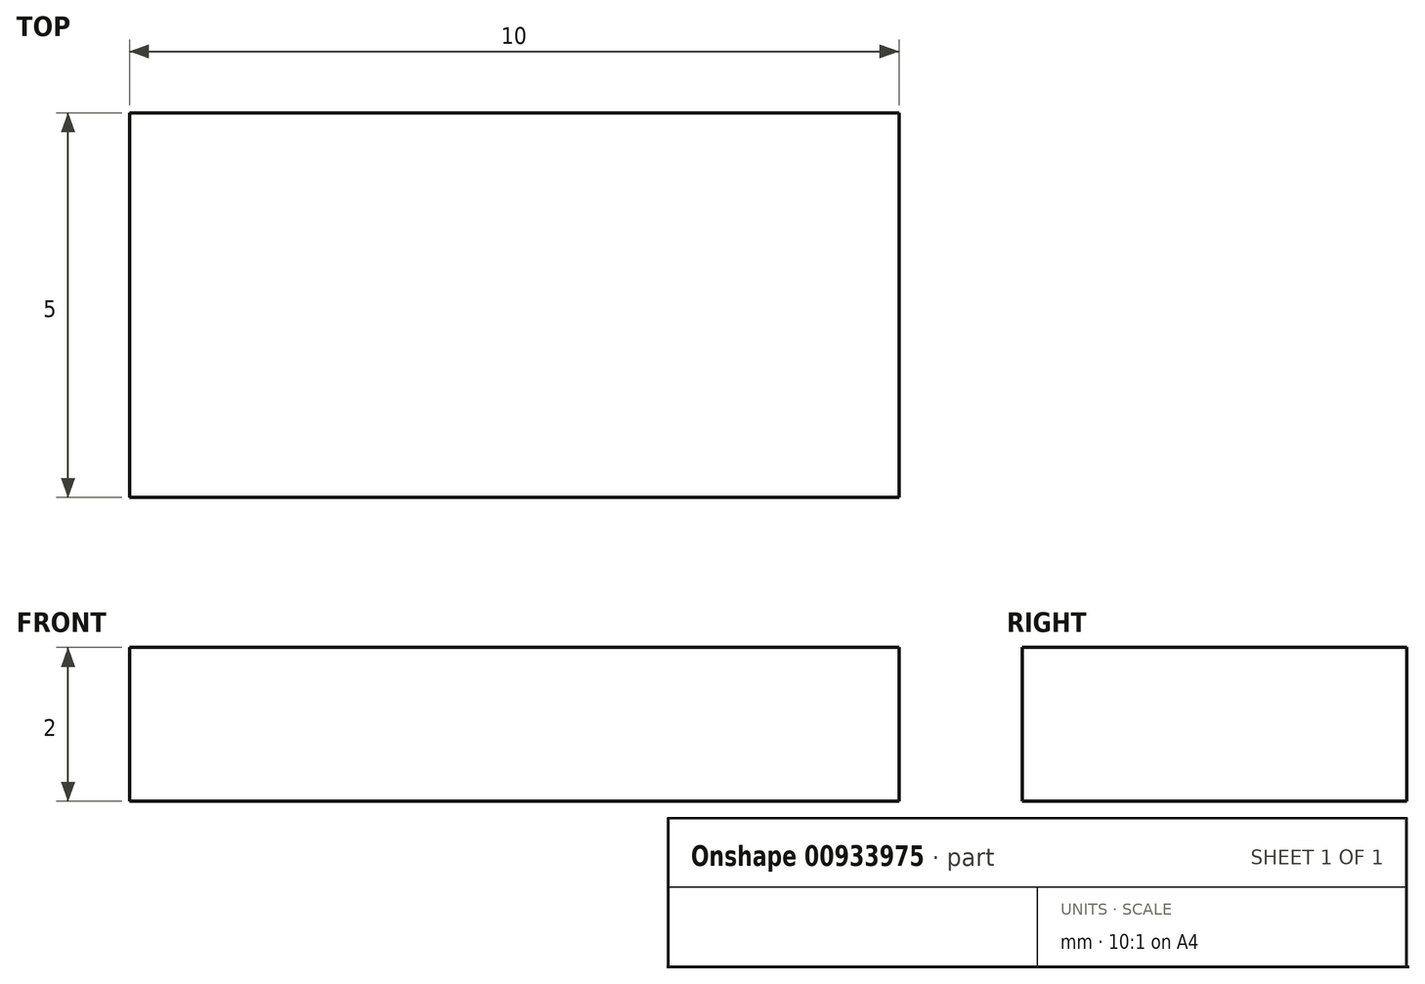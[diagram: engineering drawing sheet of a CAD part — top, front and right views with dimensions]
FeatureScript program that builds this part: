
annotation { "Feature Type Name" : "Feature", "Feature Type Description" : "" }
export const myFeature = defineFeature(function(context is Context, id is Id, definition is map)
    precondition{}
    {
        {
            var Q0;
            Q0=qCreatedBy(makeId("Top.planeOp"),FACE);
            var sketch = newSketch(context, id + "F0", { "sketchPlane" : qUnion([Q0])});
            skLineSegment(sketch, "E0.bottom", {"start": v(5, -2.5) * mm, "end": v(-5, -2.5) * mm});
            skLineSegment(sketch, "E0.top", {"start": v(5, 2.5) * mm, "end": v(-5, 2.5) * mm});
            skLineSegment(sketch, "E0.left", {"start": v(5, -2.5) * mm, "end": v(5, 2.5) * mm});
            skLineSegment(sketch, "E0.right", {"start": v(-5, -2.5) * mm, "end": v(-5, 2.5) * mm});
            skPoint(sketch, "E0.middle", {"position": v(0, 0) * mm});
            skSolve(sketch);
        }
        {
            var Q0;
            Q0 = qSketchRegion(id + "F0", true);
            extrude(context, id + "F1", {"entities" : qUnion([Q0]), "depth" : 2 * mm, "offsetDistance" : 25 * mm});
        }
    });
